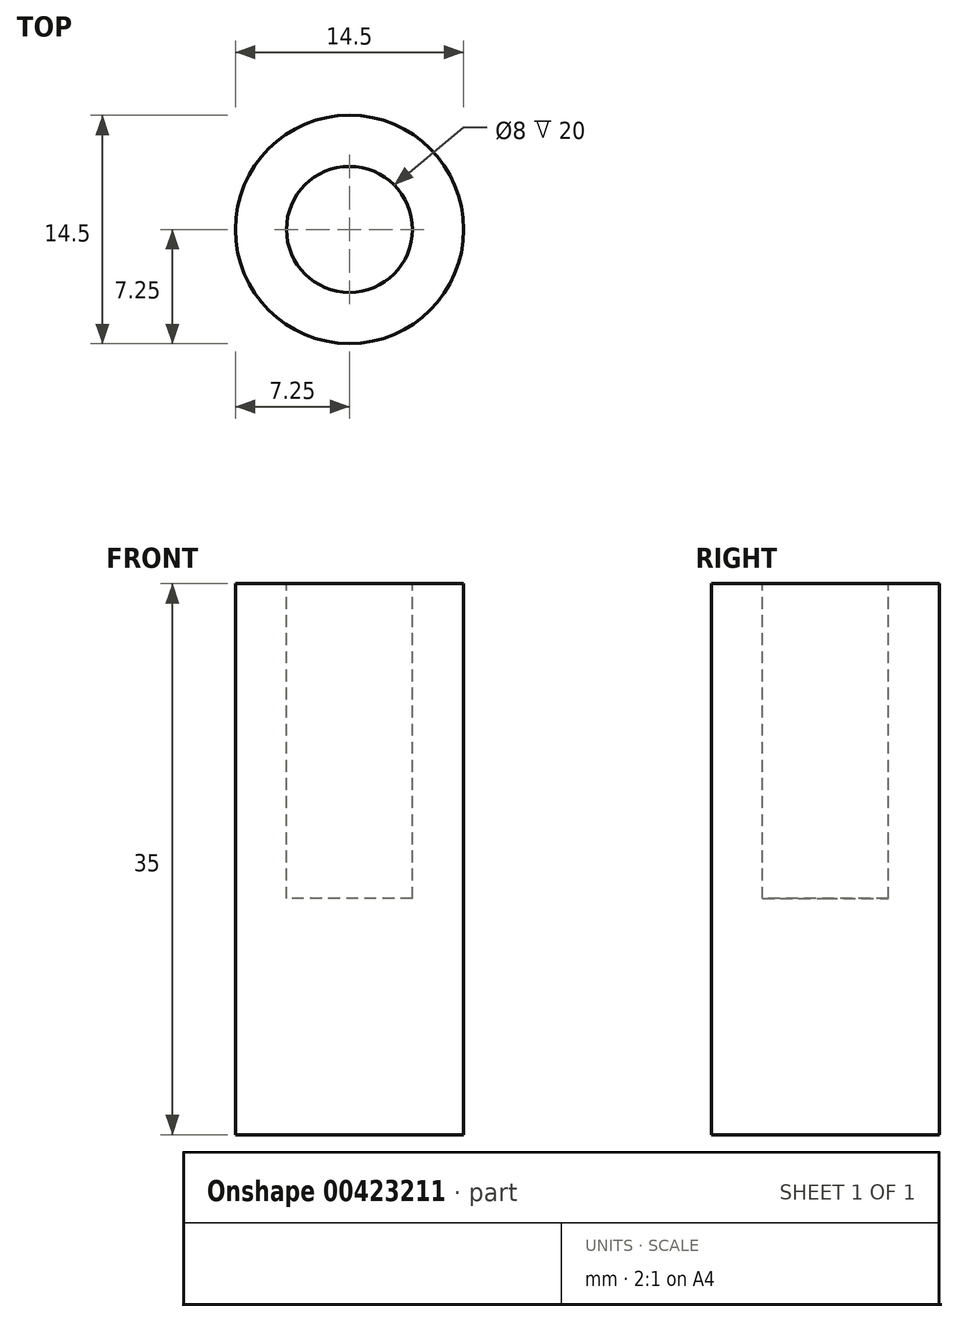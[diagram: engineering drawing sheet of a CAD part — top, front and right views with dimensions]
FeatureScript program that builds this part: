
annotation { "Feature Type Name" : "Feature", "Feature Type Description" : "" }
export const myFeature = defineFeature(function(context is Context, id is Id, definition is map)
    precondition{}
    {
        {
            var Q0;
            Q0=qCreatedBy(makeId("Top.planeOp"),FACE);
            var sketch = newSketch(context, id + "F0", { "sketchPlane" : qUnion([Q0])});
            skCircle(sketch, "E0", {"center": v(0, 0) * mm, "radius": 7.25 * mm});
            skSolve(sketch);
        }
        {
            var Q0;
            Q0=makeQuery(id+"F0.imprint","IMPRINT",FACE,{"disambiguationData":[TD([[makeQuery(id+"F0.imprint","IMPRINT",EDGE,{"derivedFrom":sQuery(id+"F0.wireOp",EDGE,"E0")}),1.0]])]});
            extrude(context, id + "F1", {"entities" : qUnion([Q0]), "depth" : 35 * mm, "offsetDistance" : 25 * mm});
        }
        {
            var Q0;
            Q0=makeQuery(id+"F1.opExtrude","CAP_FACE",FACE,{"disambiguationData":[OSD([sQuery(id+"F0.wireOp",EDGE,"E0")])],"isStart":false});
            var sketch = newSketch(context, id + "F2", { "sketchPlane" : qUnion([Q0])});
            skCircle(sketch, "E1", {"center": v(0, 0) * mm, "radius": 4 * mm});
            skSolve(sketch);
        }
        {
            var Q0;
            Q0 = qSketchRegion(id + "F2", true);
            extrude(context, id + "F3", {"entities" : qUnion([Q0]), "operationType" : NewBodyOperationType.REMOVE, "oppositeDirection" : true, "depth" : 20 * mm, "offsetDistance" : 25 * mm});
        }
    });
